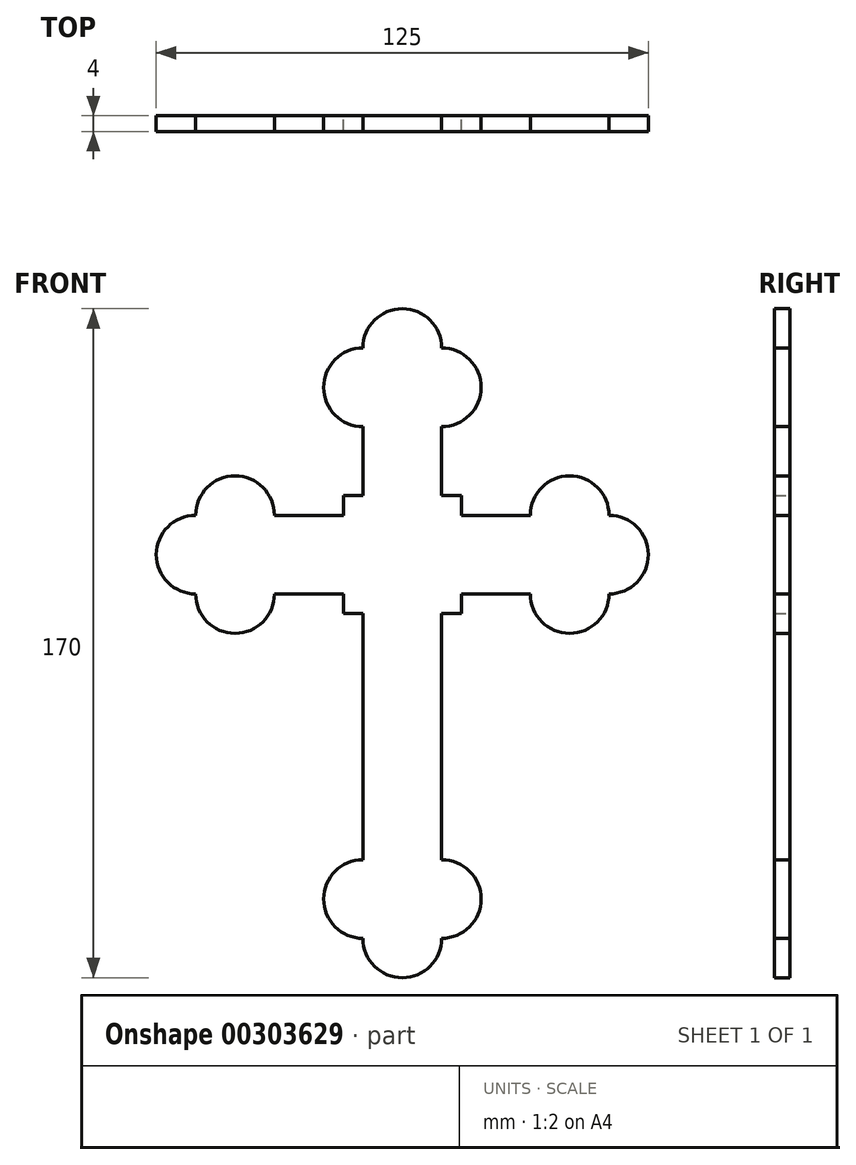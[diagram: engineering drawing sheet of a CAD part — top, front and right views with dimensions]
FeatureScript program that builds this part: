
annotation { "Feature Type Name" : "Feature", "Feature Type Description" : "" }
export const myFeature = defineFeature(function(context is Context, id is Id, definition is map)
    precondition{}
    {
        {
            var Q0;
            Q0=qCreatedBy(makeId("Front.planeOp"),FACE);
            var sketch = newSketch(context, id + "F0", { "sketchPlane" : qUnion([Q0])});
            skLineSegment(sketch, "E0.MirrorCS", {"start": v(-15, 12.5) * mm, "end": v(-32.5, 12.5) * mm});
            skLineSegment(sketch, "E1.MirrorCS", {"start": v(-32.5, 32.5) * mm, "end": v(-15, 32.5) * mm});
            skArc(sketch, "E2", {"start": v(-52.5, 32.5) * mm, "mid": v(-62.5, 22.5) * mm, "end": v(-52.5, 12.5) * mm});
            skArc(sketch, "E3", {"start": v(-32.5, 32.5) * mm, "mid": v(-42.5, 42.5) * mm, "end": v(-52.5, 32.5) * mm});
            skArc(sketch, "E4", {"start": v(-52.5, 12.5) * mm, "mid": v(-42.5, 2.5) * mm, "end": v(-32.5, 12.5) * mm});
            skLineSegment(sketch, "E5.1.0", {"start": v(-10, 37.5) * mm, "end": v(-10, 55) * mm});
            skArc(sketch, "E5.1.1", {"start": v(10, 55) * mm, "mid": v(20, 65) * mm, "end": v(10, 75) * mm});
            skLineSegment(sketch, "E5.1.2", {"start": v(10, 55) * mm, "end": v(10, 37.5) * mm});
            skArc(sketch, "E5.1.3", {"start": v(-10, 75) * mm, "mid": v(-20, 65) * mm, "end": v(-10, 55) * mm});
            skArc(sketch, "E5.1.4", {"start": v(10, 75) * mm, "mid": v(0, 85) * mm, "end": v(-10, 75) * mm});
            skLineSegment(sketch, "E5.2.0", {"start": v(15, 32.5) * mm, "end": v(32.5, 32.5) * mm});
            skArc(sketch, "E5.2.1", {"start": v(32.5, 12.5) * mm, "mid": v(42.5, 2.5) * mm, "end": v(52.5, 12.5) * mm});
            skLineSegment(sketch, "E5.2.2", {"start": v(32.5, 12.5) * mm, "end": v(15, 12.5) * mm});
            skArc(sketch, "E5.2.3", {"start": v(52.5, 32.5) * mm, "mid": v(42.5, 42.5) * mm, "end": v(32.5, 32.5) * mm});
            skArc(sketch, "E5.2.4", {"start": v(52.5, 12.5) * mm, "mid": v(62.5, 22.5) * mm, "end": v(52.5, 32.5) * mm});
            skPoint(sketch, "E5.center", {"position": v(0, 22.5) * mm});
            skLineSegment(sketch, "E5.anchor1", {"start": v(0, 22.5) * mm, "end": v(-52.5, 12.5) * mm, "construction": true});
            skLineSegment(sketch, "E5.anchor2", {"start": v(0, 22.5) * mm, "end": v(52.5, 32.5) * mm, "construction": true});
            skArc(sketch, "E6.MirrorCS", {"start": v(10, -75) * mm, "mid": v(0, -85) * mm, "end": v(-10, -75) * mm});
            skArc(sketch, "E7.MirrorCS", {"start": v(-10, -75) * mm, "mid": v(-20, -65) * mm, "end": v(-10, -55) * mm});
            skArc(sketch, "E8.MirrorCS", {"start": v(10, -55) * mm, "mid": v(20, -65) * mm, "end": v(10, -75) * mm});
            skLineSegment(sketch, "E9.trimOffspring", {"start": v(-10, -55) * mm, "end": v(-10, 7.5) * mm});
            skLineSegment(sketch, "E10", {"start": v(10, 7.5) * mm, "end": v(10, -55) * mm});
            skLineSegment(sketch, "E11.bottom", {"start": v(-15, 37.5) * mm, "end": v(-10, 37.5) * mm});
            skLineSegment(sketch, "E11.top", {"start": v(-15, 7.5) * mm, "end": v(-10, 7.5) * mm});
            skLineSegment(sketch, "E11.left", {"start": v(-15, 37.5) * mm, "end": v(-15, 32.5) * mm});
            skLineSegment(sketch, "E11.right", {"start": v(15, 37.5) * mm, "end": v(15, 32.5) * mm});
            skLineSegment(sketch, "E12.trimOffspring", {"start": v(10, 37.5) * mm, "end": v(15, 37.5) * mm});
            skLineSegment(sketch, "E13.trimOffspring", {"start": v(15, 12.5) * mm, "end": v(15, 7.5) * mm});
            skLineSegment(sketch, "E14.trimOffspring", {"start": v(-15, 12.5) * mm, "end": v(-15, 7.5) * mm});
            skLineSegment(sketch, "E15.trimOffspring", {"start": v(10, 7.5) * mm, "end": v(15, 7.5) * mm});
            skSolve(sketch);
        }
        {
            var Q0;
            Q0=makeQuery(id+"F0.imprint","IMPRINT",FACE,{"disambiguationData":[TD([[makeQuery(id+"F0.imprint","IMPRINT",EDGE,{"derivedFrom":sQuery(id+"F0.wireOp",EDGE,"E0.MirrorCS")}),-1.0]])]});
            extrude(context, id + "F1", {"entities" : qUnion([Q0]), "depth" : 4 * mm});
        }
    });
